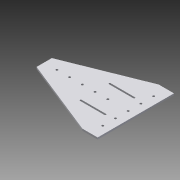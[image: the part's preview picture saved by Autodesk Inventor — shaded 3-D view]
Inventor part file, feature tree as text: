
AUTODESK INVENTOR PART (.ipt)
format: ipt  version: 2015 (Build 190159000, 159)  size: 165,376 bytes
history: native  units: in
note: dims shown in document units (in); Inventor stores cm internally (conversion verified against a paired STEP export)
features: other x5, hole x1, projected_geometry x1
ambient origin geometry x8: Origin, YZ Plane, XZ Plane, XY Plane, X Axis, Y Axis, Z Axis, Center Point
bodies: Solid1 (feature_tree)
feature tree (7):
  hole  "rivet_holes"  [1 undecoded]
  other  "face_sketch"
  other  "Plate1"
  other  "rivet_holes_sketch"
  projected_geometry  "Projected Loop1"
  other  "hm_mounting_slot_sketch"
  other  "Cut1"
note: 1 required parameter value undecoded (feature->parameter linkage not recoverable at this tier; creation-order binding heuristic only, values carry confidence <= 0.55)
